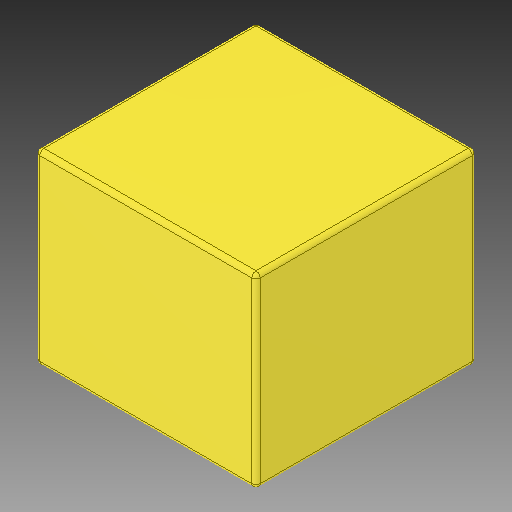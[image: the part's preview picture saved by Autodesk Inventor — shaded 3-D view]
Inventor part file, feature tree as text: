
AUTODESK INVENTOR PART (.ipt)
format: ipt  version: 2018 (Build 220112000, 112)  size: 98,304 bytes
history: native  units: in
note: dims shown in document units (in); Inventor stores cm internally (conversion verified against a paired STEP export)
features: fillet x1
ambient origin geometry x8: Origin, YZ Plane, XZ Plane, XY Plane, X Axis, Y Axis, Z Axis, Center Point
bodies: Solid1 (feature_tree)
feature tree (1):
  fillet  "Fillet1"  [1 undecoded]
note: 1 required parameter value undecoded (feature->parameter linkage not recoverable at this tier; creation-order binding heuristic only, values carry confidence <= 0.55)
